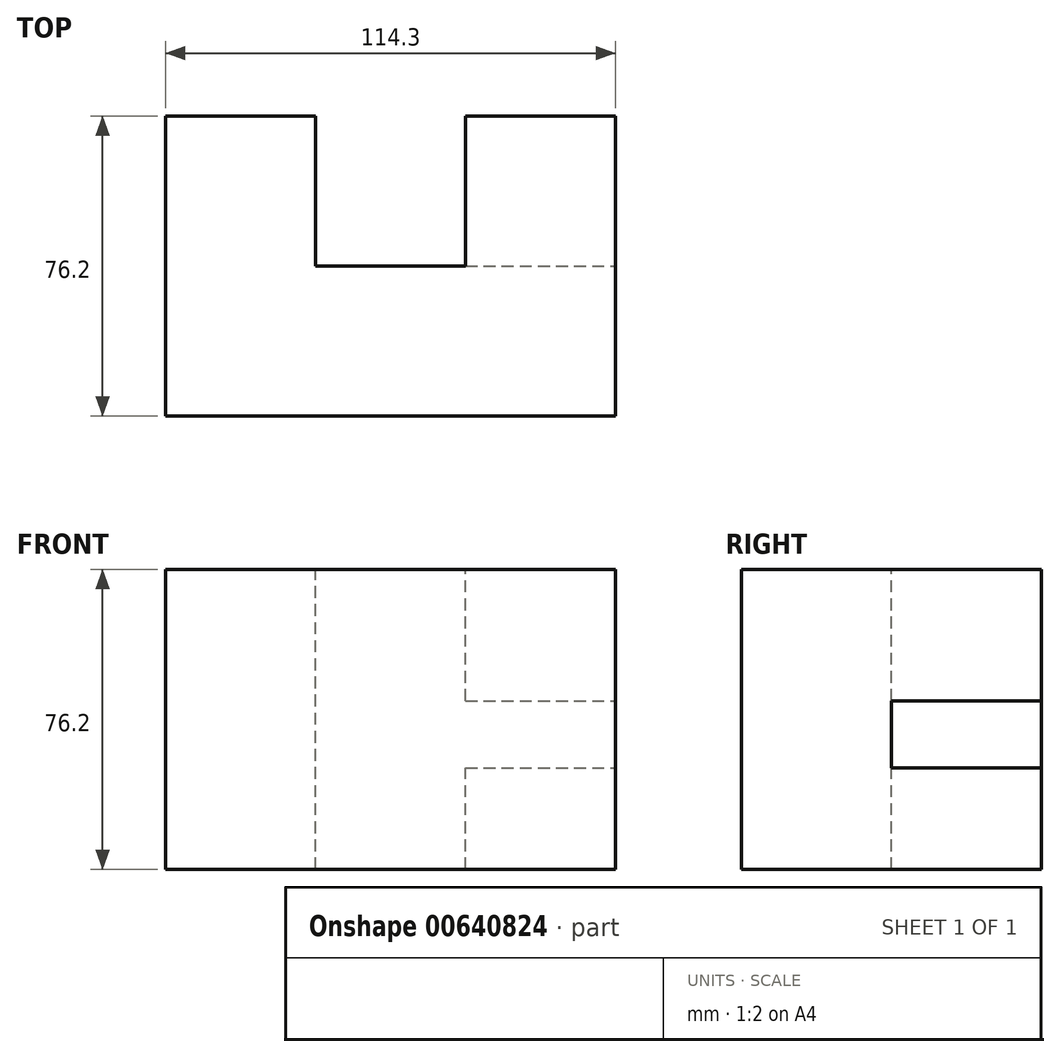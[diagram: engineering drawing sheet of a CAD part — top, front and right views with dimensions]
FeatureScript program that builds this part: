
annotation { "Feature Type Name" : "Feature", "Feature Type Description" : "" }
export const myFeature = defineFeature(function(context is Context, id is Id, definition is map)
    precondition{}
    {
        {
            var Q0;
            Q0=qCreatedBy(makeId("Top.planeOp"),FACE);
            var sketch = newSketch(context, id + "F0", { "sketchPlane" : qUnion([Q0])});
            skLineSegment(sketch, "E0", {"start": v(-57.44, 43.3) * mm, "end": v(-19.34, 43.3) * mm});
            skLineSegment(sketch, "E1", {"start": v(-57.44, 43.3) * mm, "end": v(-57.44, -32.9) * mm});
            skLineSegment(sketch, "E2", {"start": v(-57.44, -32.9) * mm, "end": v(56.86, -32.9) * mm});
            skLineSegment(sketch, "E3", {"start": v(56.86, -32.9) * mm, "end": v(56.86, 43.3) * mm});
            skLineSegment(sketch, "E4", {"start": v(56.86, 43.3) * mm, "end": v(18.76, 43.3) * mm});
            skLineSegment(sketch, "E5", {"start": v(18.76, 43.3) * mm, "end": v(18.76, 5.2) * mm});
            skLineSegment(sketch, "E6", {"start": v(18.76, 5.2) * mm, "end": v(-19.34, 5.2) * mm});
            skLineSegment(sketch, "E7", {"start": v(-19.34, 43.3) * mm, "end": v(-19.34, 5.2) * mm});
            skSolve(sketch);
        }
        {
            var Q0;
            Q0=makeQuery(id+"F0.imprint","IMPRINT",FACE,{"disambiguationData":[TD([[makeQuery(id+"F0.imprint","IMPRINT",EDGE,{"derivedFrom":sQuery(id+"F0.wireOp",EDGE,"E0")}),-1.0]])]});
            extrude(context, id + "F1", {"entities" : qUnion([Q0]), "oppositeDirection" : true, "depth" : 76.2 * mm, "offsetDistance" : 25.4 * mm});
        }
        {
            var Q0;
            Q0=makeQuery(id+"F1.opExtrude","SWEPT_FACE",FACE,{"disambiguationData":[OSD([sQuery(id+"F0.wireOp",EDGE,"E4")])]});
            var sketch = newSketch(context, id + "F2", { "sketchPlane" : qUnion([Q0])});
            skLineSegment(sketch, "E8", {"start": v(-18.76, -33.38) * mm, "end": v(-56.86, -33.38) * mm});
            skLineSegment(sketch, "E9", {"start": v(-18.76, -50.46) * mm, "end": v(-56.86, -50.46) * mm});
            skLineSegment(sketch, "E10", {"start": v(-56.86, -50.46) * mm, "end": v(-56.86, -34.5) * mm});
            skLineSegment(sketch, "E11", {"start": v(-18.76, -50.46) * mm, "end": v(-18.76, -33.38) * mm});
            skLineSegment(sketch, "E12", {"start": v(-56.86, -34.5) * mm, "end": v(-56.86, -33.38) * mm});
            skSolve(sketch);
        }
        {
            var Q0;
            Q0=makeQuery(id+"F2.imprint","IMPRINT",FACE,{"disambiguationData":[TD([[makeQuery(id+"F2.imprint","IMPRINT",EDGE,{"derivedFrom":sQuery(id+"F2.wireOp",EDGE,"E8")}),1.0]])]});
            extrude(context, id + "F3", {"entities" : qUnion([Q0]), "operationType" : NewBodyOperationType.REMOVE, "oppositeDirection" : true, "depth" : 38.1 * mm, "offsetDistance" : 25.4 * mm});
        }
    });
